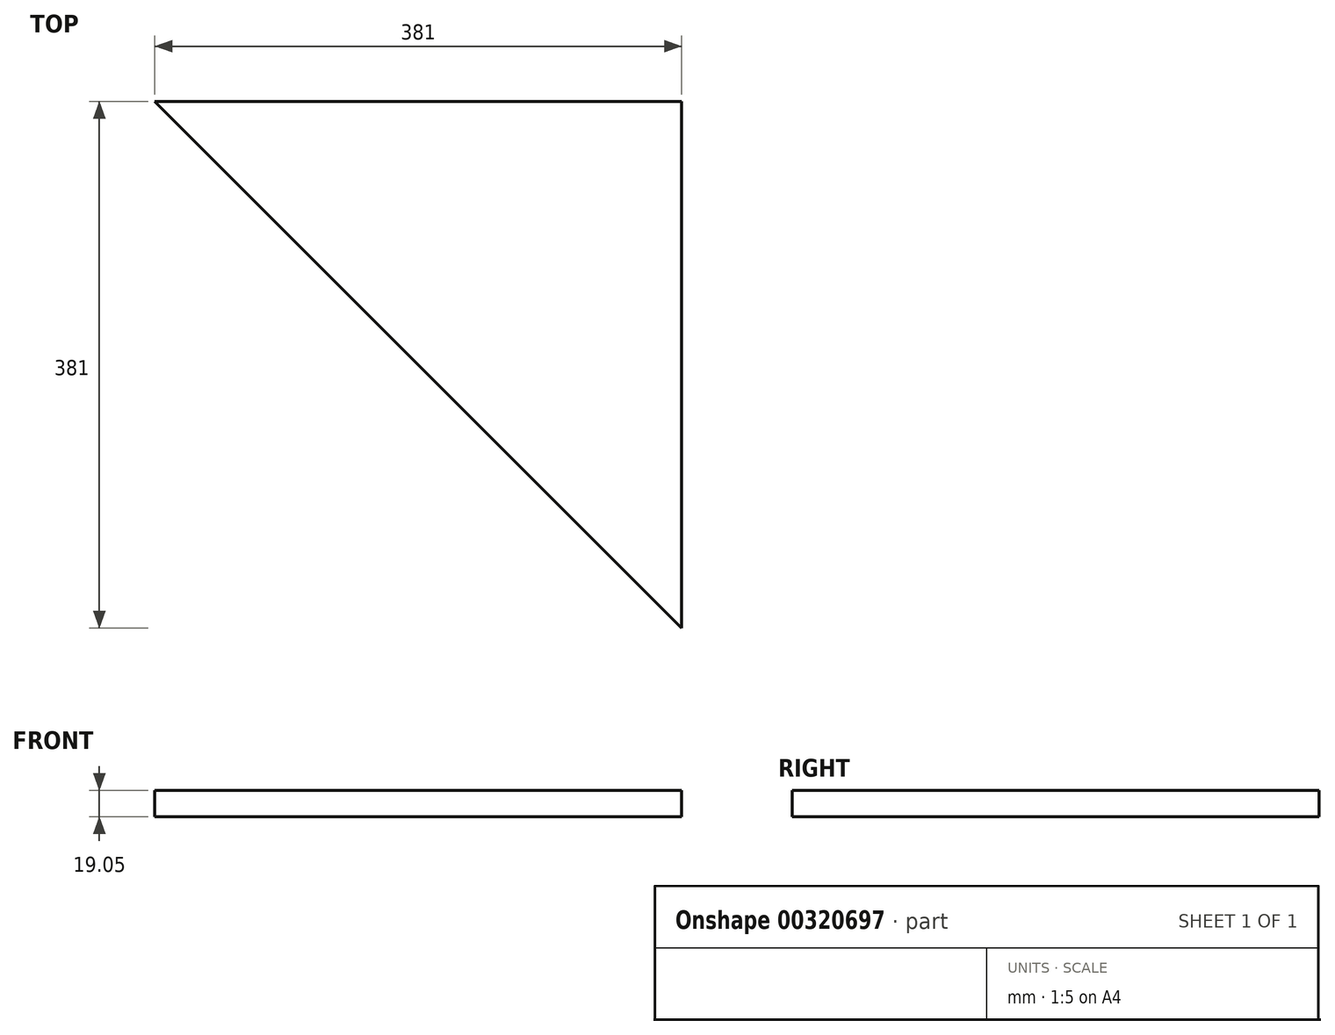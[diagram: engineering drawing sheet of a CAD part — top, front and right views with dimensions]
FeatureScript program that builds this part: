
annotation { "Feature Type Name" : "Feature", "Feature Type Description" : "" }
export const myFeature = defineFeature(function(context is Context, id is Id, definition is map)
    precondition{}
    {
        {
            var Q0;
            Q0=qCreatedBy(makeId("Top.planeOp"),FACE);
            var sketch = newSketch(context, id + "F0", { "sketchPlane" : qUnion([Q0])});
            skLineSegment(sketch, "E0", {"start": v(8, 182.28) * mm, "end": v(8, -198.72) * mm});
            skLineSegment(sketch, "E1", {"start": v(8, 182.28) * mm, "end": v(-373, 182.28) * mm});
            skLineSegment(sketch, "E2", {"start": v(-373, 182.28) * mm, "end": v(8, -198.72) * mm});
            skSolve(sketch);
        }
        {
            var Q0;
            Q0 = qSketchRegion(id + "F0", true);
            extrude(context, id + "F1", {"entities" : qUnion([Q0]), "depth" : 19.05 * mm});
        }
    });
